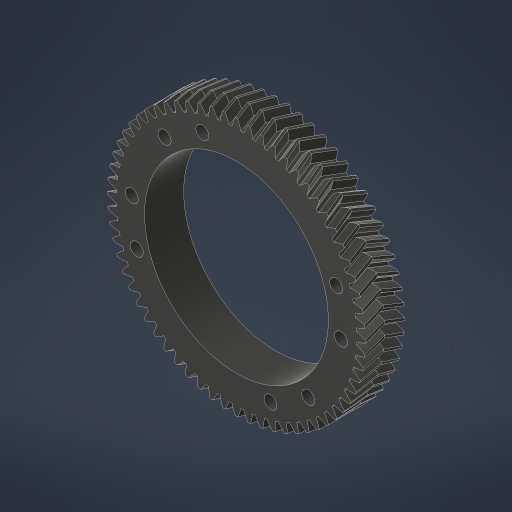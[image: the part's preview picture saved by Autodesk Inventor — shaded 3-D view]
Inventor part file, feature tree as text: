
AUTODESK INVENTOR PART (.ipt)
format: ipt  version: 2023.4 (Build 274418000, 418)  size: 1,685,504 bytes
history: native  units: in
note: dims shown in document units (in); Inventor stores cm internally (conversion verified against a paired STEP export)
features: other x3, sketch x2, hole x2, pattern_circular x1, extrude x1, projected_geometry x1
ambient origin geometry x8: Origin, YZ Plane, XZ Plane, XY Plane, X Axis, Y Axis, Z Axis, Center Point
bodies: Solid1 (feature_tree)
feature tree (10):
  other  "Helical 2M 64T"
  sketch  "Sketch1"  dims[d0=4.7244in d1=3.7in]
  other  "Work Axis1"
  hole  "Hole1"  [1 undecoded]
  pattern_circular  "Circular Pattern1"  Count=4  [1 undecoded]
  extrude  "Extrusion1"  Depth=39.3701in TaperAngle=0.0deg
  other  "DIAMETRIC PITCH"
  hole  "Hole2"  [1 undecoded]
  sketch  "Sketch3"  dims[d2=0.26in d3=29.5276in d4=0.748in d5=0.1969in d6=0.563in d7=39.3701in d8=0.8108in d9=1.5748in d10=2.4737in d12=1.0in d13=0.0in d14=5.0394in d15=1.5in d16=135.0deg d17=0.26in d18=0.38in d19=0.385in d20=0.25in d21=0.5635in d22=1.0in d23=0.8108in d25=2.122in]
  projected_geometry  "Project Cut Edges1"
note: 3 required parameter values undecoded (feature->parameter linkage not recoverable at this tier; creation-order binding heuristic only, values carry confidence <= 0.55)
